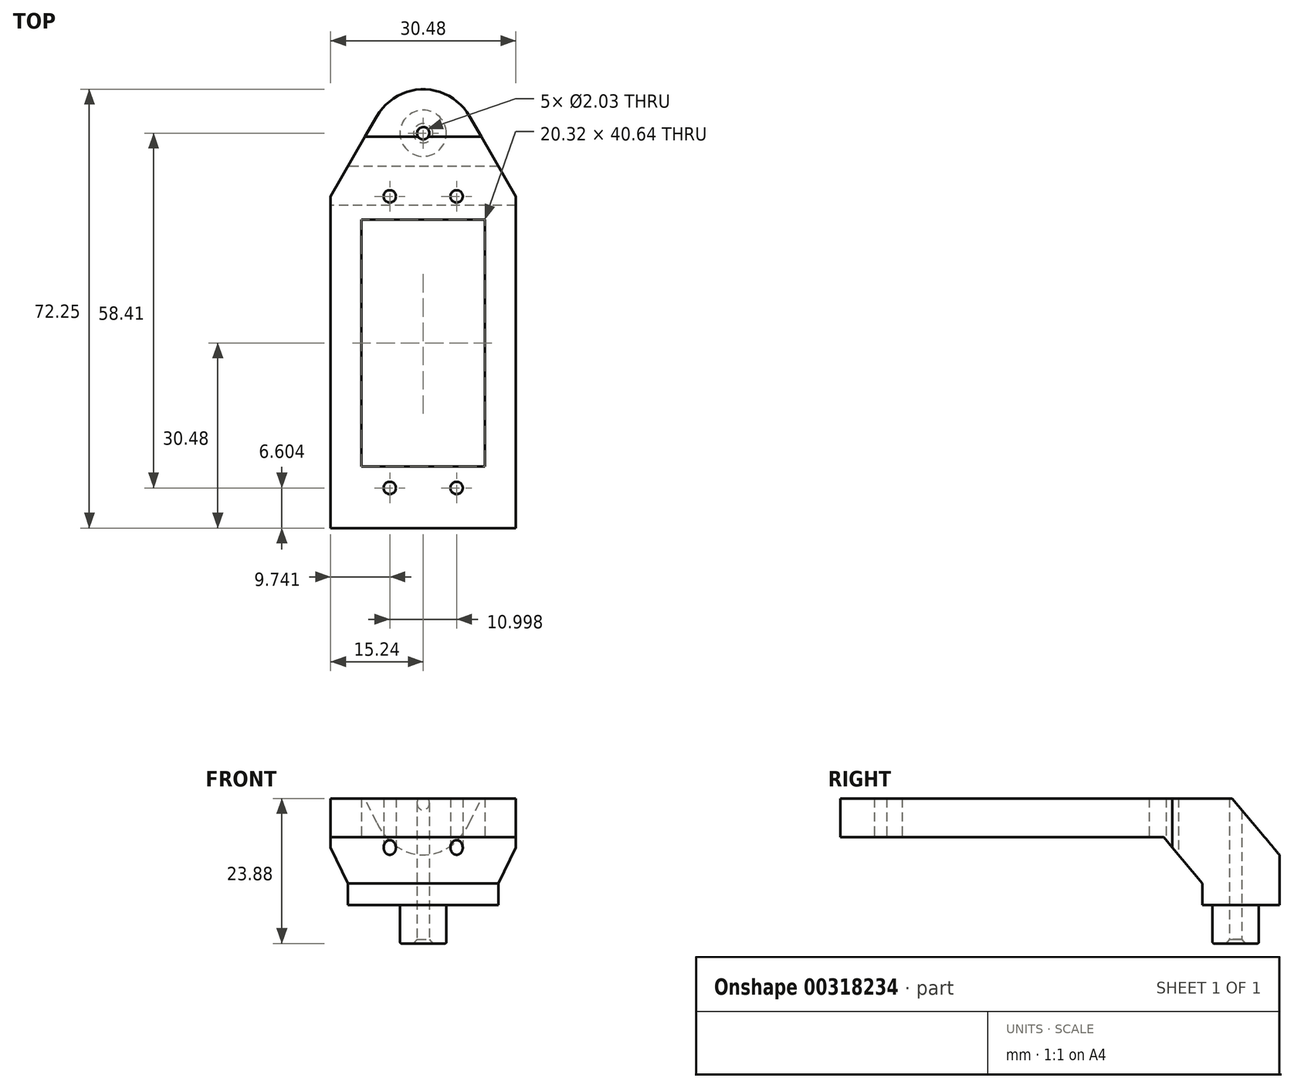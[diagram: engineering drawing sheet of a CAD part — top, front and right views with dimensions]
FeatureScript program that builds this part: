
annotation { "Feature Type Name" : "Feature", "Feature Type Description" : "" }
export const myFeature = defineFeature(function(context is Context, id is Id, definition is map)
    precondition{}
    {
        {
            var Q0;
            Q0=qCreatedBy(makeId("Top.planeOp"),FACE);
            var sketch = newSketch(context, id + "F0", { "sketchPlane" : qUnion([Q0])});
            skCircle(sketch, "E0", {"center": v(0, 0) * mm, "radius": 6.35 * mm, "construction": true});
            skCircle(sketch, "E1", {"center": v(0, 22.86) * mm, "radius": 3.81 * mm, "construction": true});
            skLineSegment(sketch, "E2.bottom", {"start": v(10.16, -30.48) * mm, "end": v(-10.16, -30.48) * mm});
            skLineSegment(sketch, "E2.top", {"start": v(10.16, 10.16) * mm, "end": v(-10.16, 10.16) * mm});
            skLineSegment(sketch, "E2.left", {"start": v(10.16, -30.48) * mm, "end": v(10.16, 10.16) * mm});
            skLineSegment(sketch, "E2.right", {"start": v(-10.16, -30.48) * mm, "end": v(-10.16, 10.16) * mm});
            skPoint(sketch, "E2.middle", {"position": v(0, -10.16) * mm});
            skLineSegment(sketch, "E3.bottom", {"start": v(15.24, -40.64) * mm, "end": v(-15.24, -40.64) * mm});
            skLineSegment(sketch, "E4", {"start": v(-15.24, -40.64) * mm, "end": v(-15.24, 13.97) * mm});
            skLineSegment(sketch, "E5", {"start": v(15.24, -40.64) * mm, "end": v(15.24, 13.97) * mm});
            skLineSegment(sketch, "E6", {"start": v(-15.24, 13.97) * mm, "end": v(15.24, 13.97) * mm, "construction": true});
            skLineSegment(sketch, "E7", {"start": v(0, 22.86) * mm, "end": v(0, 0) * mm, "construction": true});
            skCircle(sketch, "E8", {"center": v(-5.5, 13.97) * mm, "radius": 1.02 * mm});
            skCircle(sketch, "E9.MirrorC", {"center": v(5.5, 13.97) * mm, "radius": 1.02 * mm});
            skCircle(sketch, "E10", {"center": v(-5.5, -34.04) * mm, "radius": 1.02 * mm});
            skCircle(sketch, "E11.MirrorC", {"center": v(5.5, -34.04) * mm, "radius": 1.02 * mm});
            skLineSegment(sketch, "E12", {"start": v(-15.24, 13.97) * mm, "end": v(-7.62, 27.17) * mm});
            skLineSegment(sketch, "E13", {"start": v(15.24, 13.97) * mm, "end": v(7.62, 27.17) * mm});
            skPoint(sketch, "E14.endSnap0", {"position": v(0, -40.64) * mm});
            skArc(sketch, "E15", {"start": v(7.62, 27.17) * mm, "mid": v(0, 31.61) * mm, "end": v(-7.62, 27.17) * mm});
            skSolve(sketch);
        }
        {
            var Q0;
            Q0=qCreatedBy(makeId("Right.planeOp"),FACE);
            var sketch = newSketch(context, id + "F1", { "sketchPlane" : qUnion([Q0])});
            skLineSegment(sketch, "E16", {"start": v(18.91, 0) * mm, "end": v(18.91, 3.56) * mm});
            skLineSegment(sketch, "E17", {"start": v(18.91, 3.56) * mm, "end": v(12.52, 11.18) * mm});
            skLineSegment(sketch, "E18", {"start": v(12.52, 11.18) * mm, "end": v(-40.64, 11.18) * mm});
            skLineSegment(sketch, "E19.1", {"start": v(31.61, 8.18) * mm, "end": v(23.77, 17.53) * mm});
            skLineSegment(sketch, "E19.2", {"start": v(31.61, 0) * mm, "end": v(31.61, 8.18) * mm});
            skLineSegment(sketch, "E20", {"start": v(23.77, 17.53) * mm, "end": v(-40.64, 17.53) * mm});
            skLineSegment(sketch, "E21", {"start": v(-40.64, 17.53) * mm, "end": v(-40.64, 11.18) * mm});
            skLineSegment(sketch, "E22", {"start": v(18.91, 0) * mm, "end": v(31.61, 0) * mm});
            skSolve(sketch);
        }
        {
            var Q0;
            Q0 = qSketchRegion(id + "F0", true);
            var Q1;
            Q1=sQuery(id+"F1.wireOp",VERTEX,"E20.start");
            extrude(context, id + "F2", {"entities" : qUnion([Q0]), "endBound" : BoundingType.UP_TO_VERTEX, "endBoundEntityVertex" : qUnion([Q1]), "depth" : 25.4 * mm});
        }
        {
            var Q0;
            Q0 = qSketchRegion(id + "F1", true);
            extrude(context, id + "F3", {"entities" : qUnion([Q0]), "operationType" : NewBodyOperationType.INTERSECT, "endBound" : BoundingType.THROUGH_ALL, "depth" : 25.4 * mm, "hasSecondDirection" : true, "secondDirectionOppositeDirection" : true, "secondDirectionDepth" : 25.4 * mm});
        }
        {
            var Q0;
            Q0=makeQuery(id+"F0.imprint","IMPRINT",FACE,{"disambiguationData":[TD([[makeQuery(id+"F0.imprint","IMPRINT",EDGE,{"derivedFrom":sQuery(id+"F0.wireOp",EDGE,"E2.bottom")}),1.0]])]});
            var sketch = newSketch(context, id + "F4", { "sketchPlane" : qUnion([Q0])});
            skCircle(sketch, "E23", {"center": v(0, 24.37) * mm, "radius": 3.81 * mm});
            skSolve(sketch);
        }
        {
            var Q0;
            Q0=makeQuery(id+"F4.imprint","IMPRINT",FACE,{"disambiguationData":[TD([[makeQuery(id+"F4.imprint","IMPRINT",EDGE,{"derivedFrom":sQuery(id+"F4.wireOp",EDGE,"E23")}),1.0]])]});
            extrude(context, id + "F5", {"entities" : qUnion([Q0]), "operationType" : NewBodyOperationType.ADD, "oppositeDirection" : true, "depth" : 6.35 * mm});
        }
        {
            var Q0;
            Q0=makeQuery(id+"F5.opExtrude","CAP_FACE",FACE,{"disambiguationData":[OSD([sQuery(id+"F4.wireOp",EDGE,"E23")])],"isStart":false});
            var sketch = newSketch(context, id + "F6", { "sketchPlane" : qUnion([Q0])});
            skPoint(sketch, "E24", {"position": v(0, -24.37) * mm});
            skSolve(sketch);
        }
        {
            var Q0;
            Q0=sQuery(id+"F6.wireOp",VERTEX,"E24");
            var Q1;
            Q1=makeQuery(id+"F2.opExtrude","SWEPT_BODY",BODY,{"disambiguationData":[OSD([sQuery(id+"F0.wireOp",EDGE,"E2.bottom"),sQuery(id+"F0.wireOp",EDGE,"E2.top"),sQuery(id+"F0.wireOp",EDGE,"E2.left"),sQuery(id+"F0.wireOp",EDGE,"E2.right"),sQuery(id+"F0.wireOp",EDGE,"E3.bottom"),sQuery(id+"F0.wireOp",EDGE,"E4"),sQuery(id+"F0.wireOp",EDGE,"E5"),sQuery(id+"F0.wireOp",EDGE,"E8"),sQuery(id+"F0.wireOp",EDGE,"E9.MirrorC"),sQuery(id+"F0.wireOp",EDGE,"E10"),sQuery(id+"F0.wireOp",EDGE,"E11.MirrorC"),sQuery(id+"F0.wireOp",EDGE,"E12"),sQuery(id+"F0.wireOp",EDGE,"E13"),sQuery(id+"F0.wireOp",EDGE,"E15")])]});
            hole(context, id + "F7", {"style" : HoleStyle.C_SINK, "endStyle" : HoleEndStyle.THROUGH, "holeDiameter" : 2.03 * mm, "cSinkDiameter" : 3.17 * mm, "cSinkAngle" : 82 * degree, "tappedDepth" : 12.7 * mm, "tapClearance" : 3, "locations" : qUnion([Q0]), "scope" : qUnion([Q1])});
        }
        {
            var Q0;
            Q0=makeQuery(id+"F5.opExtrude","CAP_EDGE",EDGE,{"disambiguationData":[OSD([sQuery(id+"F4.wireOp",EDGE,"E23")])],"isStart":false});
            fillet(context, id + "F8", {"entities" : qUnion([Q0]), "radius" : 0.25 * mm, "tangentPropagation" : true, "allowEdgeOverflow" : false});
        }
    });
